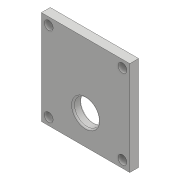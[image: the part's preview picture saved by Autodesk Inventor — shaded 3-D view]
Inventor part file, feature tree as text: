
AUTODESK INVENTOR PART (.ipt)
format: ipt  version: 2018 (Build 220112000, 112)  size: 131,584 bytes
history: native  units: mm
features: extrude x2, sketch x2, other x1, fillet x1
ambient origin geometry x8: Origin, YZ Plane, XZ Plane, XY Plane, X Axis, Y Axis, Z Axis, Center Point
bodies: Body1 (feature_tree)
feature tree (6):
  other  "Sólido2"
  extrude  "Extrusión2"  Depth=10.0mm
  fillet  "Empalme1"  [1 undecoded]
  extrude  "Extrusion4"  Depth=10.0mm
  sketch  "Boceto1"  dims[d0=30.0mm d1=10.0mm d2=0.0mm]
  sketch  "Sketch4"  dims[d3=12.0mm d4=10.0mm d5=10.0mm d6=0.0mm d10=8.5mm d11=3.0mm d12=0.0mm d13=0.5mm d20=2.5mm d21=2.5mm d22=2.5mm d23=2.5mm d24=2.5mm d25=2.5mm d26=2.5mm d27=2.5mm d28=3.0mm d29=3.0mm d30=3.0mm d31=3.0mm d32=10.0mm d33=0.0mm]
note: 1 required parameter value undecoded (feature->parameter linkage not recoverable at this tier; creation-order binding heuristic only, values carry confidence <= 0.55)
